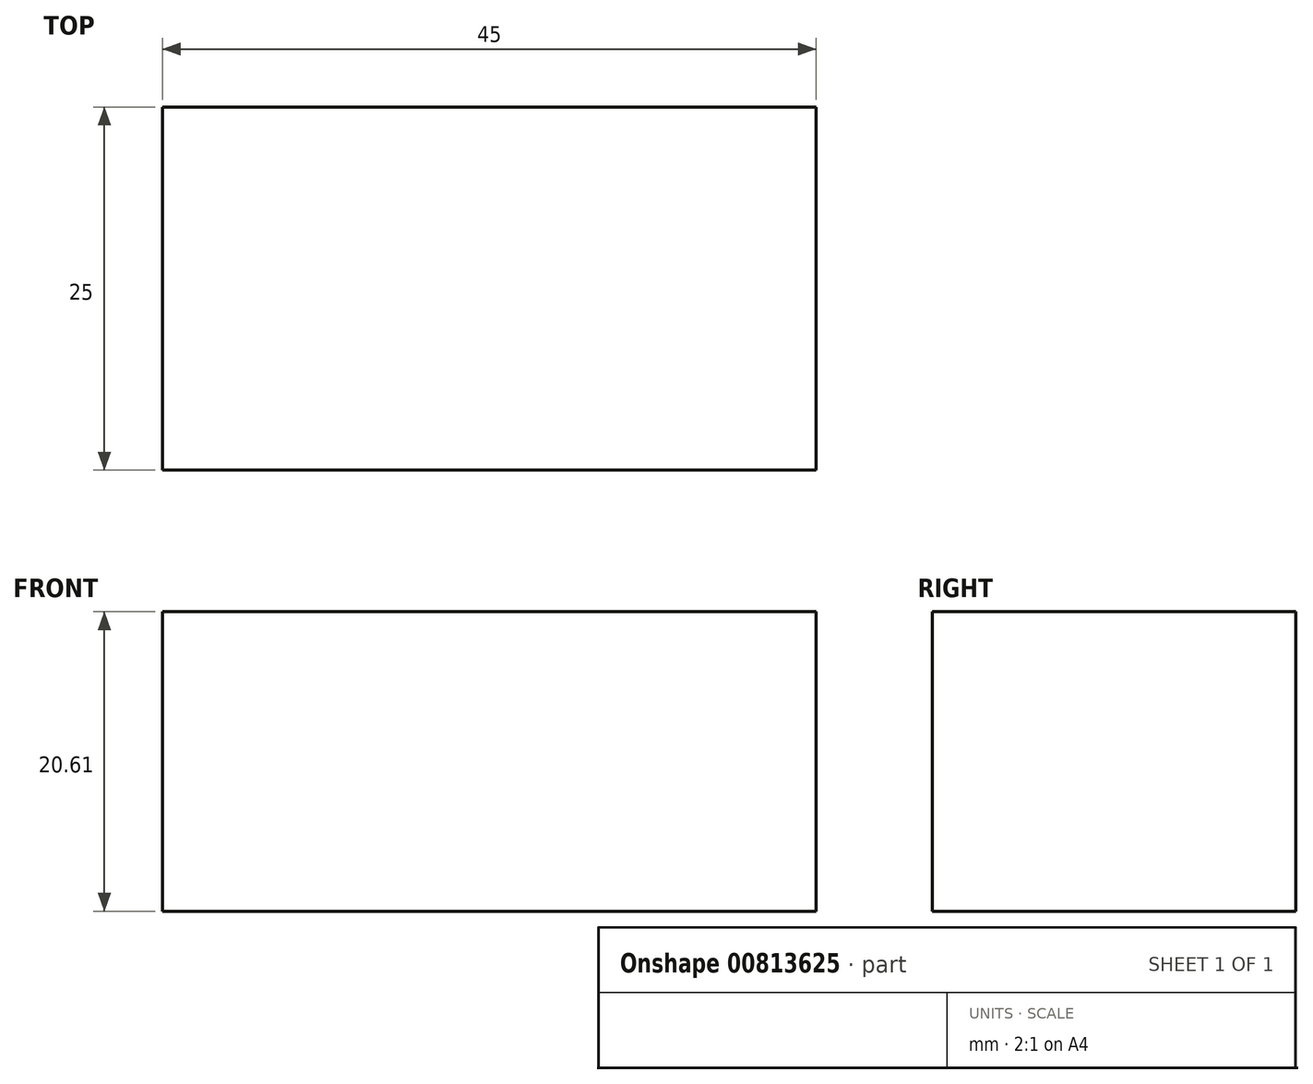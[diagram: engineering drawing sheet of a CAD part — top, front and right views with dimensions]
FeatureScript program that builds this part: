
annotation { "Feature Type Name" : "Feature", "Feature Type Description" : "" }
export const myFeature = defineFeature(function(context is Context, id is Id, definition is map)
    precondition{}
    {
        {
            var Q0;
            Q0=qCreatedBy(makeId("Front.planeOp"),FACE);
            var sketch = newSketch(context, id + "F0", { "sketchPlane" : qUnion([Q0])});
            skCircle(sketch, "E0", {"center": v(-136.47, 8.38) * mm, "radius": 27.89 * mm});
            skLineSegment(sketch, "E1.bottom", {"start": v(-92.05, 71.76) * mm, "end": v(-47.05, 71.76) * mm});
            skLineSegment(sketch, "E1.top", {"start": v(-92.05, 51.15) * mm, "end": v(-47.05, 51.15) * mm});
            skLineSegment(sketch, "E1.left", {"start": v(-92.05, 71.76) * mm, "end": v(-92.05, 51.15) * mm});
            skLineSegment(sketch, "E1.right", {"start": v(-47.05, 71.76) * mm, "end": v(-47.05, 51.15) * mm});
            skSolve(sketch);
        }
        {
            var Q0;
            Q0 = qSketchRegion(id + "F0", true);
            extrude(context, id + "F1", {"entities" : qUnion([Q0]), "depth" : 25 * mm, "offsetDistance" : 25 * mm});
        }
        {
            var Q0;
            Q0=makeQuery(id+"F1.opExtrude","SWEPT_BODY",BODY,{"disambiguationData":[OSD([sQuery(id+"F0.wireOp",EDGE,"E0")])]});
            deleteBodies(context, id + "F2", {"entities" : qUnion([Q0])});
        }
    });
